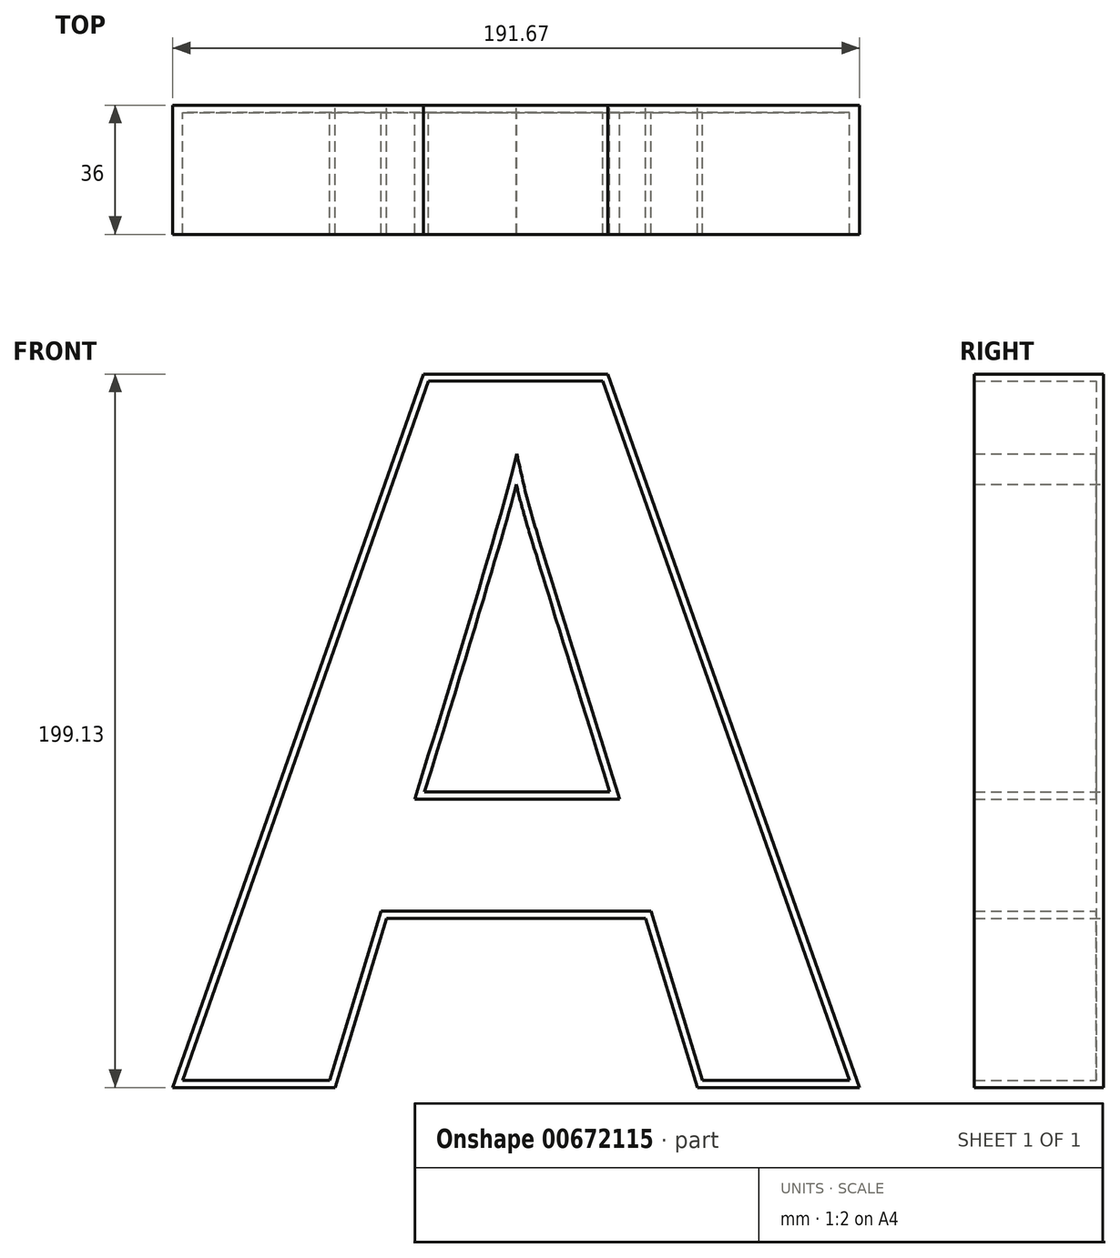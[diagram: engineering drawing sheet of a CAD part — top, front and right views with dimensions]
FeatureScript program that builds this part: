
annotation { "Feature Type Name" : "Feature", "Feature Type Description" : "" }
export const myFeature = defineFeature(function(context is Context, id is Id, definition is map)
    precondition{}
    {
        {
            var Q0;
            Q0=qCreatedBy(makeId("Front.planeOp"),FACE);
            var sketch = newSketch(context, id + "F0", { "sketchPlane" : qUnion([Q0])});
            skText(sketch, "E0", { "text": "A", "fontName": "OpenSans-Bold.ttf"});
            const initialGuessF0  = {"E0": [-0.0956, -0.10242, 1, 0, 0.2]};
            skSetInitialGuess(sketch, initialGuessF0);
            skSolve(sketch);
        }
        {
            var Q0;
            Q0=makeQuery(id+"F0.imprint","IMPRINT",FACE,{"disambiguationData":[TD([[makeQuery(id+"F0.imprint","IMPRINT",EDGE,{"derivedFrom":sQuery(id+"F0.wireOp",EDGE,"E0.sketch_text.stroke-0")}),-1.0]])]});
            extrude(context, id + "F1", {"entities" : qUnion([Q0]), "flatOperationType" : FlatOperationType.REMOVE, "depth" : 36 * mm, "offsetDistance" : 25 * mm, "domain" : OperationDomain.MODEL});
        }
        {
            var Q0;
            Q0=makeQuery(id+"F1.opExtrude","CAP_FACE",FACE,{"disambiguationData":[OSD([sQuery(id+"F0.wireOp",EDGE,"E0.sketch_text.stroke-0"),sQuery(id+"F0.wireOp",EDGE,"E0.sketch_text.stroke-1"),sQuery(id+"F0.wireOp",EDGE,"E0.sketch_text.stroke-2"),sQuery(id+"F0.wireOp",EDGE,"E0.sketch_text.stroke-3"),sQuery(id+"F0.wireOp",EDGE,"E0.sketch_text.stroke-4"),sQuery(id+"F0.wireOp",EDGE,"E0.sketch_text.stroke-5"),sQuery(id+"F0.wireOp",EDGE,"E0.sketch_text.stroke-6"),sQuery(id+"F0.wireOp",EDGE,"E0.sketch_text.stroke-7"),sQuery(id+"F0.wireOp",EDGE,"E0.sketch_text.stroke-8"),sQuery(id+"F0.wireOp",EDGE,"E0.sketch_text.stroke-9"),sQuery(id+"F0.wireOp",EDGE,"E0.sketch_text.stroke-10"),sQuery(id+"F0.wireOp",EDGE,"E0.sketch_text.stroke-11")])],"isStart":false});
            shell(context, id + "F2", {"entities" : qUnion([Q0]), "thickness" : 2 * mm});
        }
    });
